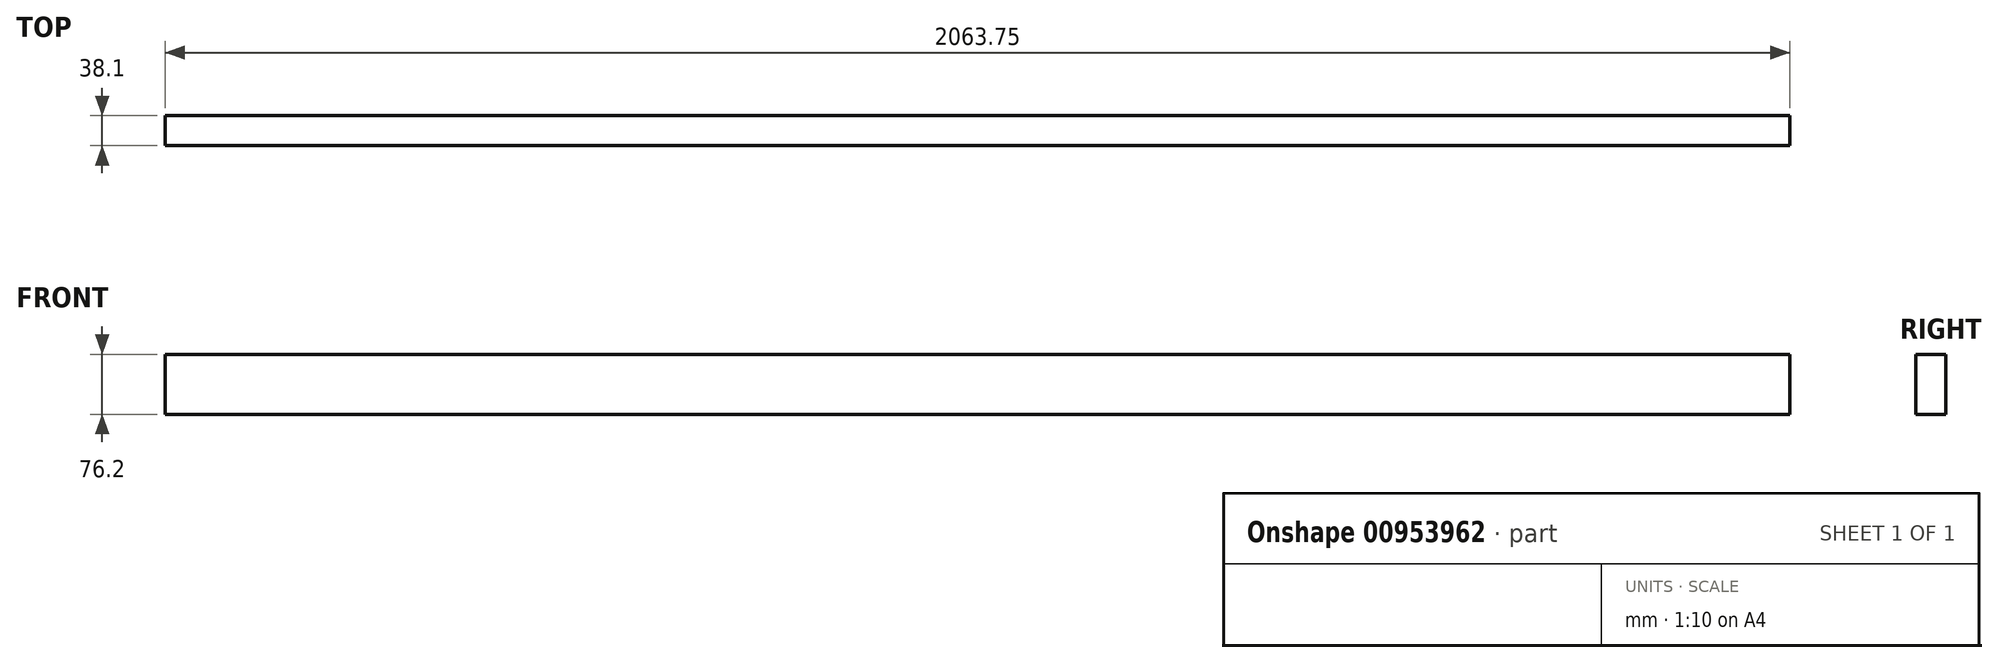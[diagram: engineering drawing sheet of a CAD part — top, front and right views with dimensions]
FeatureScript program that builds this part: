
annotation { "Feature Type Name" : "Feature", "Feature Type Description" : "" }
export const myFeature = defineFeature(function(context is Context, id is Id, definition is map)
    precondition{}
    {
        {
            var Q0;
            Q0=qCreatedBy(makeId("Front.planeOp"),FACE);
            var sketch = newSketch(context, id + "F0", { "sketchPlane" : qUnion([Q0])});
            skLineSegment(sketch, "E0.bottom", {"start": v(0, 0) * mm, "end": v(2063.75, 0) * mm});
            skLineSegment(sketch, "E0.top", {"start": v(0, 76.2) * mm, "end": v(2063.75, 76.2) * mm});
            skLineSegment(sketch, "E0.left", {"start": v(0, 0) * mm, "end": v(0, 76.2) * mm});
            skLineSegment(sketch, "E0.right", {"start": v(2063.75, 0) * mm, "end": v(2063.75, 76.2) * mm});
            skSolve(sketch);
        }
        {
            var Q0;
            Q0=makeQuery(id+"F0.imprint","IMPRINT",FACE,{"disambiguationData":[TD([[makeQuery(id+"F0.imprint","IMPRINT",EDGE,{"derivedFrom":sQuery(id+"F0.wireOp",EDGE,"E0.bottom")}),1.0]])]});
            extrude(context, id + "F1", {"entities" : qUnion([Q0]), "depth" : 38.1 * mm, "offsetDistance" : 25.4 * mm});
        }
    });
